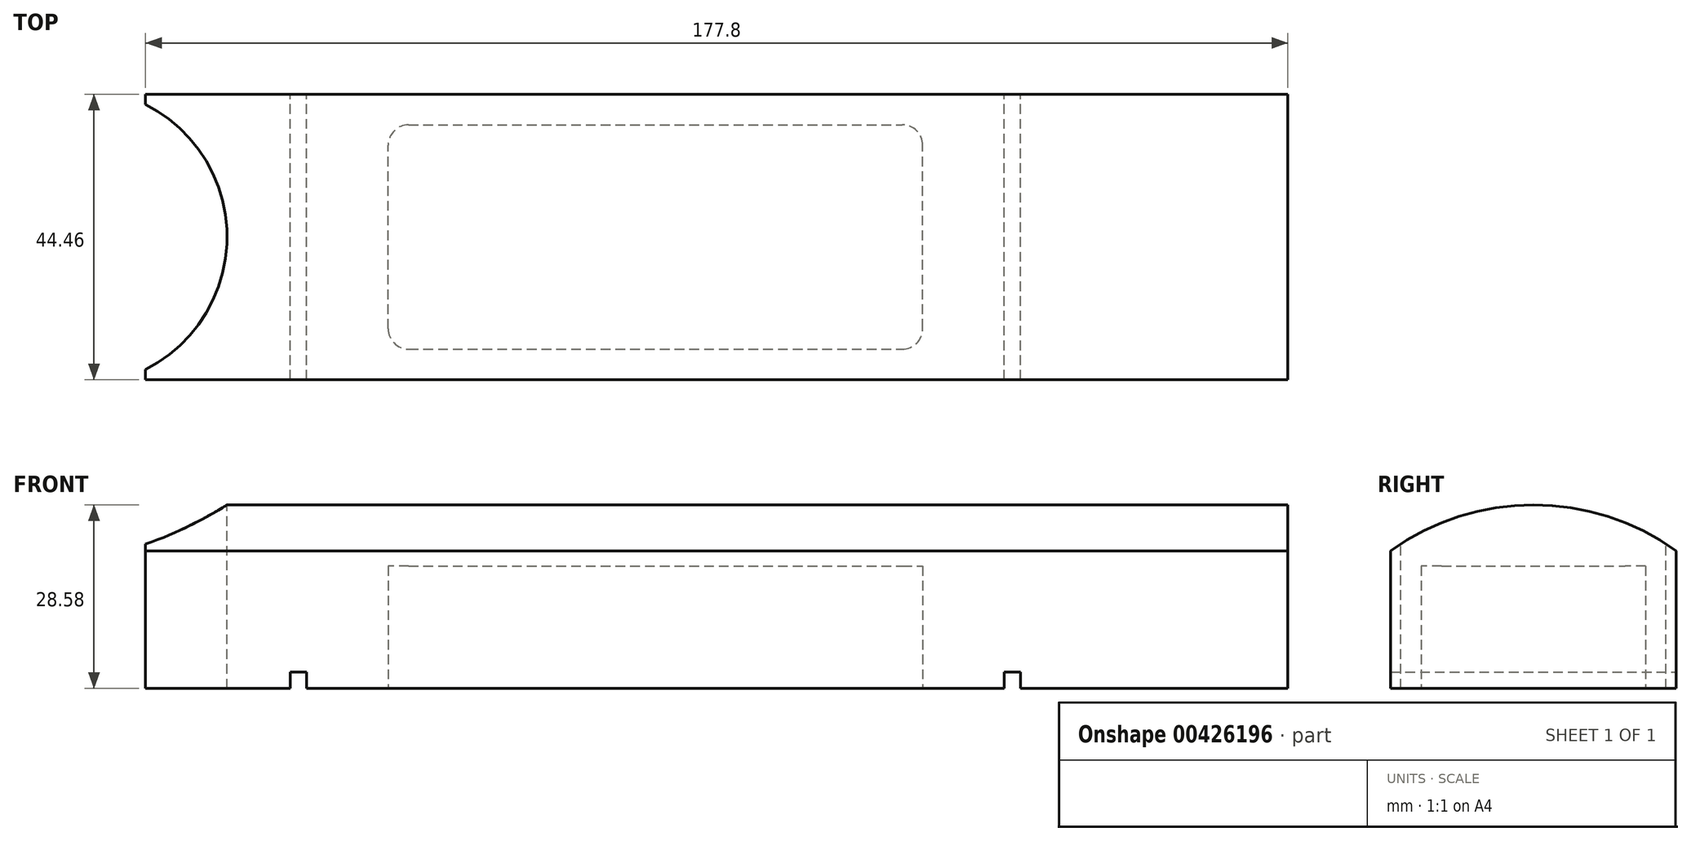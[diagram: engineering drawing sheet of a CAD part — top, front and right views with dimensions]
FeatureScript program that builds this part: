
annotation { "Feature Type Name" : "Feature", "Feature Type Description" : "" }
export const myFeature = defineFeature(function(context is Context, id is Id, definition is map)
    precondition{}
    {
        {
            var Q0;
            Q0=qCreatedBy(makeId("Front.planeOp"),FACE);
            var sketch = newSketch(context, id + "F0", { "sketchPlane" : qUnion([Q0])});
            skLineSegment(sketch, "E0.bottom", {"start": v(-88.9, -15.88) * mm, "end": v(88.9, -15.88) * mm});
            skLineSegment(sketch, "E0.top", {"start": v(-88.9, 15.88) * mm, "end": v(88.9, 15.88) * mm});
            skLineSegment(sketch, "E0.left", {"start": v(-88.9, -15.88) * mm, "end": v(-88.9, 15.88) * mm});
            skLineSegment(sketch, "E0.right", {"start": v(88.9, -15.88) * mm, "end": v(88.9, 15.88) * mm});
            skLineSegment(sketch, "E1", {"start": v(-88.9, 15.88) * mm, "end": v(88.9, -15.88) * mm, "construction": true});
            skPoint(sketch, "E2", {"position": v(0, 0) * mm});
            skSolve(sketch);
        }
        {
            var Q0;
            Q0=makeQuery(id+"F0.imprint","IMPRINT",FACE,{"disambiguationData":[TD([[makeQuery(id+"F0.imprint","IMPRINT",EDGE,{"derivedFrom":sQuery(id+"F0.wireOp",EDGE,"E0.bottom")}),1.0]])]});
            extrude(context, id + "F11", {"entities" : qUnion([Q0]), "endBound" : BoundingType.SYMMETRIC, "depth" : 44.45 * mm});
        }
        {
            var Q0;
            Q0=qCreatedBy(makeId("Front.planeOp"),FACE);
            var sketch = newSketch(context, id + "F1", { "sketchPlane" : qUnion([Q0])});
            skLineSegment(sketch, "E3.0", {"start": v(-88.9, -15.88) * mm, "end": v(88.9, -15.88) * mm, "construction": true});
            skLineSegment(sketch, "E4.bottom", {"start": v(-66.36, -15.88) * mm, "end": v(-63.82, -15.88) * mm});
            skLineSegment(sketch, "E4.top", {"start": v(-66.36, -13.34) * mm, "end": v(-63.82, -13.34) * mm});
            skLineSegment(sketch, "E4.left", {"start": v(-66.36, -15.88) * mm, "end": v(-66.36, -13.34) * mm});
            skLineSegment(sketch, "E4.right", {"start": v(-63.82, -15.88) * mm, "end": v(-63.82, -13.34) * mm});
            skLineSegment(sketch, "E5.bottom", {"start": v(44.77, -15.88) * mm, "end": v(47.3, -15.88) * mm});
            skLineSegment(sketch, "E5.top", {"start": v(44.77, -13.34) * mm, "end": v(47.3, -13.34) * mm});
            skLineSegment(sketch, "E5.left", {"start": v(44.77, -15.88) * mm, "end": v(44.77, -13.34) * mm});
            skLineSegment(sketch, "E5.right", {"start": v(47.3, -15.88) * mm, "end": v(47.3, -13.34) * mm});
            skPoint(sketch, "E6", {"position": v(-65.09, -15.88) * mm});
            skPoint(sketch, "E7", {"position": v(46.04, -15.88) * mm});
            skSolve(sketch);
        }
        {
            var Q0;
            Q0=qSketchRegion(id+"F1",true);
            extrude(context, id + "F2", {"entities" : qUnion([Q0]), "operationType" : NewBodyOperationType.REMOVE, "endBound" : BoundingType.UP_TO_NEXT, "depth" : 50.8 * mm, "hasSecondDirection" : true, "secondDirectionBound" : SecondDirectionBoundingType.UP_TO_NEXT, "secondDirectionOppositeDirection" : true, "secondDirectionDepth" : 25.4 * mm});
        }
        {
            var Q0;
            Q0=makeQuery(id+"F11.opExtrude","SWEPT_FACE",FACE,{"disambiguationData":[OSD([sQuery(id+"F0.wireOp",EDGE,"E0.top")])]});
            var sketch = newSketch(context, id + "F3", { "sketchPlane" : qUnion([Q0])});
            skArc(sketch, "E8", {"start": v(-88.9, -20.64) * mm, "mid": v(-76.2, 0) * mm, "end": v(-88.9, 20.64) * mm});
            skLineSegment(sketch, "E9", {"start": v(-76.2, -22.23) * mm, "end": v(-76.2, 22.23) * mm, "construction": true});
            skLineSegment(sketch, "E10", {"start": v(-88.9, -20.64) * mm, "end": v(-88.9, 20.64) * mm});
            skSolve(sketch);
        }
        {
            var Q0;
            Q0=makeQuery(id+"F3.imprint","IMPRINT",FACE,{"disambiguationData":[TD([[makeQuery(id+"F3.imprint","IMPRINT",EDGE,{"derivedFrom":sQuery(id+"F3.wireOp",EDGE,"E8")}),1.0]])]});
            extrude(context, id + "F4", {"entities" : qUnion([Q0]), "operationType" : NewBodyOperationType.REMOVE, "endBound" : BoundingType.THROUGH_ALL, "oppositeDirection" : true, "depth" : 25.4 * mm});
        }
        {
            var Q0;
            Q0=makeQuery(id+"F11.opExtrude","SWEPT_FACE",FACE,{"disambiguationData":[OSD([sQuery(id+"F0.wireOp",EDGE,"E0.right")])]});
            var sketch = newSketch(context, id + "F5", { "sketchPlane" : qUnion([Q0])});
            skArc(sketch, "E11", {"start": v(22.22, 5.55) * mm, "mid": v(0, 12.7) * mm, "end": v(-22.23, 5.55) * mm});
            skPoint(sketch, "E12", {"position": v(0, -15.87) * mm});
            skLineSegment(sketch, "E13", {"start": v(-22.23, 12.7) * mm, "end": v(22.23, 12.7) * mm, "construction": true});
            skLineSegment(sketch, "E14", {"start": v(-22.23, 5.55) * mm, "end": v(-22.23, 15.88) * mm});
            skLineSegment(sketch, "E15", {"start": v(-22.23, 15.88) * mm, "end": v(22.23, 15.88) * mm});
            skLineSegment(sketch, "E16", {"start": v(22.23, 15.88) * mm, "end": v(22.22, 5.55) * mm});
            skSolve(sketch);
        }
        {
            var Q0;
            Q0=makeQuery(id+"F5.imprint","IMPRINT",FACE,{"disambiguationData":[TD([[makeQuery(id+"F5.imprint","IMPRINT",EDGE,{"derivedFrom":sQuery(id+"F5.wireOp",EDGE,"E11")}),-1.0]])]});
            extrude(context, id + "F6", {"entities" : qUnion([Q0]), "operationType" : NewBodyOperationType.REMOVE, "endBound" : BoundingType.THROUGH_ALL, "oppositeDirection" : true, "depth" : 25.4 * mm});
        }
        {
            var Q0;
            {var subQ3=sQuery(id+"F0.wireOp",EDGE,"E0.bottom");Q0=makeQuery(id+"F2.boolean.opBoolean","SPLIT",FACE,{"disambiguationData":[TD([makeQuery(id+"F2.opExtrude","SWEPT_FACE",FACE,{"disambiguationData":[OSD([sQuery(id+"F1.wireOp",EDGE,"E4.right")])]})])],"derivedFrom":makeQuery(id+"F11.opExtrude","SWEPT_FACE",FACE,{"disambiguationData":[OSD([subQ3])]})});}
            var sketch = newSketch(context, id + "F7", { "sketchPlane" : qUnion([Q0])});
            skLineSegment(sketch, "E17.bottom", {"start": v(-51.12, 17.46) * mm, "end": v(32.07, 17.46) * mm});
            skLineSegment(sketch, "E17.top", {"start": v(-51.12, -17.46) * mm, "end": v(32.07, -17.46) * mm});
            skLineSegment(sketch, "E17.left", {"start": v(-51.12, 17.46) * mm, "end": v(-51.12, -17.46) * mm});
            skLineSegment(sketch, "E17.right", {"start": v(32.07, 17.46) * mm, "end": v(32.07, -17.46) * mm});
            skSolve(sketch);
        }
        {
            var Q0;
            Q0=makeQuery(id+"F7.imprint","IMPRINT",FACE,{"disambiguationData":[TD([[makeQuery(id+"F7.imprint","IMPRINT",EDGE,{"derivedFrom":sQuery(id+"F7.wireOp",EDGE,"E17.bottom")}),-1.0]])]});
            extrude(context, id + "F8", {"entities" : qUnion([Q0]), "operationType" : NewBodyOperationType.REMOVE, "oppositeDirection" : true, "depth" : 19.05 * mm});
        }
        {
            var Q0;
            Q0=makeQuery(id+"F8.boolean.opBoolean","COPY",EDGE,{"derivedFrom":makeQuery(id+"F8.opExtrude","SWEPT_EDGE",EDGE,{"disambiguationData":[OSD([sQuery(id+"F7.wireOp",EDGE,"E17.bottom"),sQuery(id+"F7.wireOp",EDGE,"E17.right")])]})});
            var Q1;
            Q1=makeQuery(id+"F8.boolean.opBoolean","COPY",EDGE,{"derivedFrom":makeQuery(id+"F8.opExtrude","SWEPT_EDGE",EDGE,{"disambiguationData":[OSD([sQuery(id+"F7.wireOp",EDGE,"E17.bottom"),sQuery(id+"F7.wireOp",EDGE,"E17.left")])]})});
            var Q2;
            Q2=makeQuery(id+"F8.boolean.opBoolean","COPY",EDGE,{"derivedFrom":makeQuery(id+"F8.opExtrude","SWEPT_EDGE",EDGE,{"disambiguationData":[OSD([sQuery(id+"F7.wireOp",EDGE,"E17.top"),sQuery(id+"F7.wireOp",EDGE,"E17.left")])]})});
            var Q3;
            Q3=makeQuery(id+"F8.boolean.opBoolean","COPY",EDGE,{"derivedFrom":makeQuery(id+"F8.opExtrude","SWEPT_EDGE",EDGE,{"disambiguationData":[OSD([sQuery(id+"F7.wireOp",EDGE,"E17.top"),sQuery(id+"F7.wireOp",EDGE,"E17.right")])]})});
            fillet(context, id + "F9", {"entities" : qUnion([Q0, Q1, Q2, Q3]), "radius" : 3.17 * mm, "tangentPropagation" : true, "allowEdgeOverflow" : false});
        }
    });
